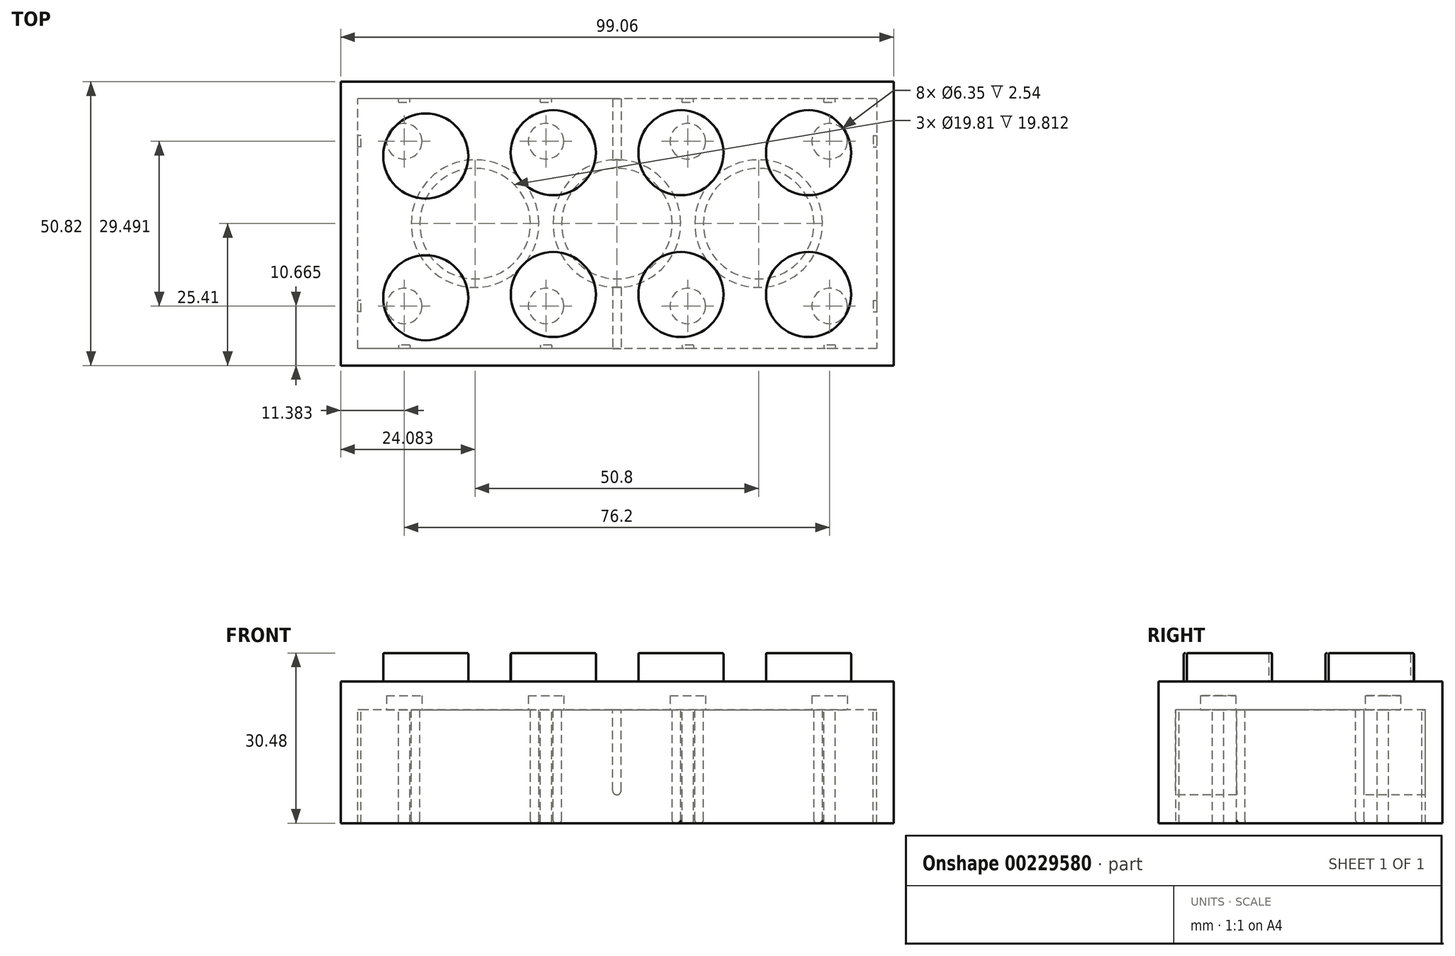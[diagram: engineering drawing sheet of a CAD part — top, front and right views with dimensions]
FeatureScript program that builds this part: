
annotation { "Feature Type Name" : "Feature", "Feature Type Description" : "" }
export const myFeature = defineFeature(function(context is Context, id is Id, definition is map)
    precondition{}
    {
        {
            var Q0;
            Q0=qCreatedBy(makeId("Top.planeOp"),FACE);
            var sketch = newSketch(context, id + "F0", { "sketchPlane" : qUnion([Q0])});
            skLineSegment(sketch, "E0.bottom", {"start": v(45.78, -25.41) * mm, "end": v(-53.28, -25.41) * mm});
            skLineSegment(sketch, "E0.top", {"start": v(45.78, 25.41) * mm, "end": v(-53.28, 25.41) * mm});
            skLineSegment(sketch, "E0.left", {"start": v(45.78, -25.41) * mm, "end": v(45.78, 25.41) * mm});
            skPoint(sketch, "E0.middle", {"position": v(0, 0) * mm});
            skLineSegment(sketch, "E1", {"start": v(-53.28, 25.41) * mm, "end": v(-53.28, -25.41) * mm});
            skSolve(sketch);
        }
        {
            var Q0;
            Q0=makeQuery(id+"F0.imprint","IMPRINT",FACE,{"disambiguationData":[TD([[makeQuery(id+"F0.imprint","IMPRINT",EDGE,{"derivedFrom":sQuery(id+"F0.wireOp",EDGE,"E0.bottom")}),-1.0]])]});
            extrude(context, id + "F1", {"entities" : qUnion([Q0]), "depth" : 25.4 * mm});
        }
        {
            var Q0;
            Q0=makeQuery(id+"F1.opExtrude","CAP_FACE",FACE,{"disambiguationData":[OSD([sQuery(id+"F0.wireOp",EDGE,"E0.bottom"),sQuery(id+"F0.wireOp",EDGE,"E0.top"),sQuery(id+"F0.wireOp",EDGE,"E0.left"),sQuery(id+"F0.wireOp",EDGE,"E0.right")])],"isStart":false});
            var sketch = newSketch(context, id + "F2", { "sketchPlane" : qUnion([Q0])});
            skCircle(sketch, "E2", {"center": v(-15.18, 12.7) * mm, "radius": 7.63 * mm});
            skCircle(sketch, "E3", {"center": v(7.68, 12.7) * mm, "radius": 7.62 * mm});
            skCircle(sketch, "E4", {"center": v(30.54, 12.7) * mm, "radius": 7.62 * mm});
            skCircle(sketch, "E5", {"center": v(30.54, -12.7) * mm, "radius": 7.62 * mm});
            skCircle(sketch, "E6", {"center": v(7.68, -12.7) * mm, "radius": 7.62 * mm});
            skCircle(sketch, "E7", {"center": v(-15.18, -12.7) * mm, "radius": 7.62 * mm});
            skCircle(sketch, "E8", {"center": v(-38.04, -13.3) * mm, "radius": 7.62 * mm});
            skCircle(sketch, "E9", {"center": v(-38.04, 12.1) * mm, "radius": 7.62 * mm});
            skLineSegment(sketch, "E10", {"start": v(-53.27, -12.48) * mm, "end": v(-53.27, -25.41) * mm});
            skLineSegment(sketch, "E11", {"start": v(-53.27, -12.48) * mm, "end": v(-53.27, 25.41) * mm});
            skSolve(sketch);
        }
        {
            var Q0;
            Q0=makeQuery(id+"F2.imprint","IMPRINT",FACE,{"disambiguationData":[TD([[makeQuery(id+"F2.imprint","IMPRINT",EDGE,{"derivedFrom":sQuery(id+"F2.wireOp",EDGE,"E2")}),1.0]])]});
            var Q1;
            Q1=makeQuery(id+"F2.imprint","IMPRINT",FACE,{"disambiguationData":[TD([[makeQuery(id+"F2.imprint","IMPRINT",EDGE,{"derivedFrom":sQuery(id+"F2.wireOp",EDGE,"E3")}),1.0]])]});
            var Q2;
            Q2=makeQuery(id+"F2.imprint","IMPRINT",FACE,{"disambiguationData":[TD([[makeQuery(id+"F2.imprint","IMPRINT",EDGE,{"derivedFrom":sQuery(id+"F2.wireOp",EDGE,"E4")}),1.0]])]});
            var Q3;
            Q3=makeQuery(id+"F2.imprint","IMPRINT",FACE,{"disambiguationData":[TD([[makeQuery(id+"F2.imprint","IMPRINT",EDGE,{"derivedFrom":sQuery(id+"F2.wireOp",EDGE,"E5")}),1.0]])]});
            var Q4;
            Q4=makeQuery(id+"F2.imprint","IMPRINT",FACE,{"disambiguationData":[TD([[makeQuery(id+"F2.imprint","IMPRINT",EDGE,{"derivedFrom":sQuery(id+"F2.wireOp",EDGE,"E6")}),1.0]])]});
            var Q5;
            Q5=makeQuery(id+"F2.imprint","IMPRINT",FACE,{"disambiguationData":[TD([[makeQuery(id+"F2.imprint","IMPRINT",EDGE,{"derivedFrom":sQuery(id+"F2.wireOp",EDGE,"E7")}),1.0]])]});
            var Q6;
            Q6=makeQuery(id+"F2.imprint","IMPRINT",FACE,{"disambiguationData":[TD([[makeQuery(id+"F2.imprint","IMPRINT",EDGE,{"derivedFrom":sQuery(id+"F2.wireOp",EDGE,"E8")}),1.0]])]});
            var Q7;
            Q7=makeQuery(id+"F2.imprint","IMPRINT",FACE,{"disambiguationData":[TD([[makeQuery(id+"F2.imprint","IMPRINT",EDGE,{"derivedFrom":sQuery(id+"F2.wireOp",EDGE,"E9")}),1.0]])]});
            extrude(context, id + "F3", {"entities" : qUnion([Q0, Q1, Q2, Q3, Q4, Q5, Q6, Q7]), "operationType" : NewBodyOperationType.ADD, "endBound" : BoundingType.SYMMETRIC, "depth" : 10.16 * mm});
        }
        {
            var Q0;
            Q0=makeQuery(id+"F1.opExtrude","CAP_FACE",FACE,{"disambiguationData":[OSD([sQuery(id+"F0.wireOp",EDGE,"E0.bottom"),sQuery(id+"F0.wireOp",EDGE,"E0.top"),sQuery(id+"F0.wireOp",EDGE,"E0.left"),sQuery(id+"F0.wireOp",EDGE,"E1")])],"isStart":true});
            var sketch = newSketch(context, id + "F4", { "sketchPlane" : qUnion([Q0])});
            skLineSegment(sketch, "E12.bottom", {"start": v(42.73, -22.37) * mm, "end": v(-50.24, -22.37) * mm});
            skLineSegment(sketch, "E13", {"start": v(42.73, -22.37) * mm, "end": v(42.73, 22.37) * mm});
            skLineSegment(sketch, "E14", {"start": v(42.73, 22.37) * mm, "end": v(-50.24, 22.37) * mm});
            skLineSegment(sketch, "E15", {"start": v(-50.24, 22.37) * mm, "end": v(-50.24, -22.37) * mm});
            skPoint(sketch, "E16.endSnap0", {"position": v(-50.24, 0) * mm});
            skSolve(sketch);
        }
        {
            var Q0;
            Q0=makeQuery(id+"F4.imprint","IMPRINT",FACE,{"disambiguationData":[TD([[makeQuery(id+"F4.imprint","IMPRINT",EDGE,{"derivedFrom":sQuery(id+"F4.wireOp",EDGE,"E12.bottom")}),-1.0]])]});
            extrude(context, id + "F5", {"entities" : qUnion([Q0]), "operationType" : NewBodyOperationType.REMOVE, "oppositeDirection" : true, "depth" : 20.32 * mm});
        }
        {
            var Q0;
            Q0=makeQuery(id+"F5.boolean.opBoolean","COPY",FACE,{"derivedFrom":makeQuery(id+"F5.opExtrude","CAP_FACE",FACE,{"disambiguationData":[OSD([sQuery(id+"F4.wireOp",EDGE,"E12.bottom"),sQuery(id+"F4.wireOp",EDGE,"E13"),sQuery(id+"F4.wireOp",EDGE,"E14"),sQuery(id+"F4.wireOp",EDGE,"E15")])],"isStart":false})});
            var sketch = newSketch(context, id + "F6", { "sketchPlane" : qUnion([Q0])});
            skPoint(sketch, "E17.endSnap0", {"position": v(-50.24, 0) * mm});
            skLineSegment(sketch, "E18.0", {"start": v(-4.56, -22.37) * mm, "end": v(-4.56, -11.4) * mm});
            skLineSegment(sketch, "E19.0", {"start": v(-3.03, -22.37) * mm, "end": v(-3.03, -11.4) * mm});
            skPoint(sketch, "E20", {"position": v(-3.8, 0) * mm});
            skCircle(sketch, "E21", {"center": v(-3.8, 0) * mm, "radius": 11.43 * mm});
            skCircle(sketch, "E22.0", {"center": v(-3.8, 0) * mm, "radius": 9.9 * mm});
            skLineSegment(sketch, "E23.trimOffspring", {"start": v(-3.03, 11.4) * mm, "end": v(-3.03, 22.37) * mm});
            skLineSegment(sketch, "E24.trimOffspring", {"start": v(-4.56, 11.4) * mm, "end": v(-4.56, 22.37) * mm});
            skPoint(sketch, "E25", {"position": v(-29.2, 0) * mm});
            skCircle(sketch, "E26", {"center": v(-29.2, 0) * mm, "radius": 9.9 * mm});
            skCircle(sketch, "E27.0", {"center": v(-29.2, 0) * mm, "radius": 11.43 * mm});
            skCircle(sketch, "E28", {"center": v(-16.5, 14.75) * mm, "radius": 3.18 * mm});
            skPoint(sketch, "E29", {"position": v(-16.5, -14.75) * mm});
            skCircle(sketch, "E30", {"center": v(-16.5, -14.75) * mm, "radius": 3.18 * mm});
            skPoint(sketch, "E31", {"position": v(-41.9, 14.75) * mm});
            skPoint(sketch, "E32", {"position": v(-41.9, -14.75) * mm});
            skCircle(sketch, "E33", {"center": v(-41.9, -14.75) * mm, "radius": 3.18 * mm});
            skCircle(sketch, "E34", {"center": v(-41.9, 14.75) * mm, "radius": 3.18 * mm});
            skCircle(sketch, "E35", {"center": v(8.9, 14.75) * mm, "radius": 3.18 * mm});
            skCircle(sketch, "E36", {"center": v(8.9, -14.75) * mm, "radius": 3.18 * mm});
            skPoint(sketch, "E37", {"position": v(21.6, 0) * mm});
            skCircle(sketch, "E38", {"center": v(21.6, 0) * mm, "radius": 9.9 * mm});
            skCircle(sketch, "E39", {"center": v(21.6, 0) * mm, "radius": 11.43 * mm});
            skCircle(sketch, "E40", {"center": v(34.3, 14.75) * mm, "radius": 3.18 * mm});
            skCircle(sketch, "E41", {"center": v(34.3, -14.75) * mm, "radius": 3.18 * mm});
            skPoint(sketch, "E42", {"position": v(-50.24, -14.75) * mm});
            skLineSegment(sketch, "E43.bottom", {"start": v(-49.63, -13.73) * mm, "end": v(-50.24, -13.73) * mm});
            skLineSegment(sketch, "E43.top", {"start": v(-49.63, -15.76) * mm, "end": v(-50.24, -15.76) * mm});
            skLineSegment(sketch, "E43.left", {"start": v(-49.63, -13.73) * mm, "end": v(-49.63, -15.76) * mm});
            skPoint(sketch, "E44", {"position": v(-50.24, -15.76) * mm});
            skPoint(sketch, "E45", {"position": v(-50.24, -13.73) * mm});
            skPoint(sketch, "E46", {"position": v(-50.24, 14.75) * mm});
            skLineSegment(sketch, "E47.bottom", {"start": v(-49.63, 15.76) * mm, "end": v(-50.24, 15.76) * mm});
            skLineSegment(sketch, "E47.top", {"start": v(-49.63, 13.73) * mm, "end": v(-50.24, 13.73) * mm});
            skLineSegment(sketch, "E47.left", {"start": v(-49.63, 15.76) * mm, "end": v(-49.63, 13.73) * mm});
            skPoint(sketch, "E48", {"position": v(-50.24, 13.73) * mm});
            skPoint(sketch, "E49", {"position": v(-50.24, 15.76) * mm});
            skPoint(sketch, "E50", {"position": v(-16.5, 22.37) * mm});
            skLineSegment(sketch, "E51.bottom", {"start": v(-15.48, 21.76) * mm, "end": v(-17.51, 21.76) * mm});
            skLineSegment(sketch, "E51.left", {"start": v(-15.48, 21.76) * mm, "end": v(-15.48, 22.37) * mm});
            skLineSegment(sketch, "E51.right", {"start": v(-17.51, 21.76) * mm, "end": v(-17.51, 22.37) * mm});
            skPoint(sketch, "E52", {"position": v(-17.51, 22.37) * mm});
            skPoint(sketch, "E53", {"position": v(-15.48, 22.37) * mm});
            skPoint(sketch, "E54", {"position": v(8.9, 22.37) * mm});
            skLineSegment(sketch, "E55.bottom", {"start": v(9.92, 21.76) * mm, "end": v(7.89, 21.76) * mm});
            skLineSegment(sketch, "E55.left", {"start": v(9.92, 21.76) * mm, "end": v(9.92, 22.37) * mm});
            skLineSegment(sketch, "E55.right", {"start": v(7.89, 21.76) * mm, "end": v(7.89, 22.37) * mm});
            skPoint(sketch, "E56", {"position": v(7.89, 22.37) * mm});
            skPoint(sketch, "E57", {"position": v(9.92, 22.37) * mm});
            skPoint(sketch, "E58", {"position": v(-41.9, 22.37) * mm});
            skLineSegment(sketch, "E59.bottom", {"start": v(-40.88, 21.76) * mm, "end": v(-42.91, 21.76) * mm});
            skLineSegment(sketch, "E59.left", {"start": v(-40.88, 21.76) * mm, "end": v(-40.88, 22.37) * mm});
            skLineSegment(sketch, "E59.right", {"start": v(-42.91, 21.76) * mm, "end": v(-42.91, 22.37) * mm});
            skPoint(sketch, "E60", {"position": v(-42.91, 22.37) * mm});
            skPoint(sketch, "E61", {"position": v(-40.88, 22.37) * mm});
            skPoint(sketch, "E62", {"position": v(34.3, 22.37) * mm});
            skLineSegment(sketch, "E63.bottom", {"start": v(35.32, 21.76) * mm, "end": v(33.29, 21.76) * mm});
            skLineSegment(sketch, "E63.left", {"start": v(35.32, 21.76) * mm, "end": v(35.32, 22.37) * mm});
            skLineSegment(sketch, "E63.right", {"start": v(33.29, 21.76) * mm, "end": v(33.29, 22.37) * mm});
            skPoint(sketch, "E64", {"position": v(33.29, 22.37) * mm});
            skPoint(sketch, "E65", {"position": v(35.32, 22.37) * mm});
            skPoint(sketch, "E66", {"position": v(42.73, 14.75) * mm});
            skLineSegment(sketch, "E67.bottom", {"start": v(42.13, 13.73) * mm, "end": v(42.73, 13.73) * mm});
            skLineSegment(sketch, "E67.top", {"start": v(42.13, 15.76) * mm, "end": v(42.73, 15.76) * mm});
            skLineSegment(sketch, "E67.left", {"start": v(42.13, 13.73) * mm, "end": v(42.13, 15.76) * mm});
            skPoint(sketch, "E68", {"position": v(42.73, 15.76) * mm});
            skPoint(sketch, "E69", {"position": v(42.73, 13.73) * mm});
            skPoint(sketch, "E70", {"position": v(42.73, -14.75) * mm});
            skLineSegment(sketch, "E71.bottom", {"start": v(42.13, -15.76) * mm, "end": v(42.73, -15.76) * mm});
            skLineSegment(sketch, "E71.top", {"start": v(42.13, -13.73) * mm, "end": v(42.73, -13.73) * mm});
            skLineSegment(sketch, "E71.left", {"start": v(42.13, -15.76) * mm, "end": v(42.13, -13.73) * mm});
            skPoint(sketch, "E72", {"position": v(42.73, -13.73) * mm});
            skPoint(sketch, "E73", {"position": v(42.73, -15.76) * mm});
            skPoint(sketch, "E74", {"position": v(34.3, -22.37) * mm});
            skLineSegment(sketch, "E75.bottom", {"start": v(33.29, -21.76) * mm, "end": v(35.32, -21.76) * mm});
            skLineSegment(sketch, "E75.left", {"start": v(33.29, -21.76) * mm, "end": v(33.29, -22.37) * mm});
            skLineSegment(sketch, "E75.right", {"start": v(35.32, -21.76) * mm, "end": v(35.32, -22.37) * mm});
            skPoint(sketch, "E76", {"position": v(35.32, -22.37) * mm});
            skPoint(sketch, "E77", {"position": v(33.29, -22.37) * mm});
            skPoint(sketch, "E78", {"position": v(8.9, -22.37) * mm});
            skLineSegment(sketch, "E79.bottom", {"start": v(7.89, -21.76) * mm, "end": v(9.92, -21.76) * mm});
            skLineSegment(sketch, "E79.left", {"start": v(7.89, -21.76) * mm, "end": v(7.89, -22.37) * mm});
            skLineSegment(sketch, "E79.right", {"start": v(9.92, -21.76) * mm, "end": v(9.92, -22.37) * mm});
            skPoint(sketch, "E80", {"position": v(9.92, -22.37) * mm});
            skPoint(sketch, "E81", {"position": v(7.89, -22.37) * mm});
            skPoint(sketch, "E82", {"position": v(-16.5, -22.37) * mm});
            skLineSegment(sketch, "E83.bottom", {"start": v(-17.51, -21.76) * mm, "end": v(-15.48, -21.76) * mm});
            skLineSegment(sketch, "E83.left", {"start": v(-17.51, -21.76) * mm, "end": v(-17.51, -22.37) * mm});
            skLineSegment(sketch, "E83.right", {"start": v(-15.48, -21.76) * mm, "end": v(-15.48, -22.37) * mm});
            skPoint(sketch, "E84", {"position": v(-15.48, -22.37) * mm});
            skPoint(sketch, "E85", {"position": v(-17.51, -22.37) * mm});
            skPoint(sketch, "E86", {"position": v(-41.9, -22.37) * mm});
            skLineSegment(sketch, "E87.bottom", {"start": v(-42.91, -21.76) * mm, "end": v(-40.88, -21.76) * mm});
            skLineSegment(sketch, "E87.left", {"start": v(-42.91, -21.76) * mm, "end": v(-42.91, -22.37) * mm});
            skLineSegment(sketch, "E87.right", {"start": v(-40.88, -21.76) * mm, "end": v(-40.88, -22.37) * mm});
            skPoint(sketch, "E88", {"position": v(-40.88, -22.37) * mm});
            skPoint(sketch, "E89", {"position": v(-42.91, -22.37) * mm});
            skSolve(sketch);
        }
        {
            var Q0;
            {var subQ0=sQuery(id+"F6.wireOp",EDGE,"E18.0");Q0=makeQuery(id+"F6.imprint","IMPRINT",FACE,{"disambiguationData":[TD([[makeQuery(id+"F6.imprint","IMPRINT",EDGE,{"derivedFrom":subQ0}),-1.0]])]});}
            extrude(context, id + "F7", {"entities" : qUnion([Q0]), "operationType" : NewBodyOperationType.ADD, "depth" : 15.24 * mm});
        }
        {
            var Q0;
            Q0=makeQuery(id+"F7.opExtrude","CAP_EDGE",EDGE,{"disambiguationData":[OSD([sQuery(id+"F6.wireOp",EDGE,"E19.0")])],"isStart":false});
            var Q1;
            Q1=makeQuery(id+"F7.opExtrude","CAP_EDGE",EDGE,{"disambiguationData":[OSD([sQuery(id+"F6.wireOp",EDGE,"E18.0")])],"isStart":false});
            fillet(context, id + "F8", {"entities" : qUnion([Q0, Q1]), "radius" : 0.76 * mm, "tangentPropagation" : true, "allowEdgeOverflow" : false});
        }
        {
            var Q0;
            {var subQ0=sQuery(id+"F6.wireOp",EDGE,"E23.trimOffspring");Q0=makeQuery(id+"F6.imprint","IMPRINT",FACE,{"disambiguationData":[TD([[makeQuery(id+"F6.imprint","IMPRINT",EDGE,{"derivedFrom":subQ0}),1.0]])]});}
            extrude(context, id + "F9", {"entities" : qUnion([Q0]), "operationType" : NewBodyOperationType.ADD, "depth" : 15.24 * mm});
        }
        {
            var Q0;
            Q0=makeQuery(id+"F9.opExtrude","CAP_EDGE",EDGE,{"disambiguationData":[OSD([sQuery(id+"F6.wireOp",EDGE,"E23.trimOffspring")])],"isStart":false});
            var Q1;
            Q1=makeQuery(id+"F9.opExtrude","CAP_EDGE",EDGE,{"disambiguationData":[OSD([sQuery(id+"F6.wireOp",EDGE,"E24.trimOffspring")])],"isStart":false});
            fillet(context, id + "F10", {"entities" : qUnion([Q0, Q1]), "radius" : 0.76 * mm, "tangentPropagation" : true, "allowEdgeOverflow" : false});
        }
        {
            var Q0;
            Q0=makeQuery(id+"F6.imprint","IMPRINT",FACE,{"disambiguationData":[TD([[makeQuery(id+"F6.imprint","IMPRINT",EDGE,{"derivedFrom":sQuery(id+"F6.wireOp",EDGE,"E22.0")}),-1.0]])]});
            var Q1;
            Q1=makeQuery(id+"F6.imprint","IMPRINT",FACE,{"disambiguationData":[TD([[makeQuery(id+"F6.imprint","IMPRINT",EDGE,{"derivedFrom":sQuery(id+"F6.wireOp",EDGE,"Xv8gO2pj-0vQc-Pp1w-HGMN-q8keW2Wz2Wm3")}),-1.0]])]});
            var Q2;
            Q2=makeQuery(id+"F6.imprint","IMPRINT",FACE,{"disambiguationData":[TD([[makeQuery(id+"F6.imprint","IMPRINT",EDGE,{"derivedFrom":sQuery(id+"F6.wireOp",EDGE,"E26")}),-1.0]])]});
            var Q3;
            Q3=makeQuery(id+"F6.imprint","IMPRINT",FACE,{"disambiguationData":[TD([[makeQuery(id+"F6.imprint","IMPRINT",EDGE,{"derivedFrom":sQuery(id+"F6.wireOp",EDGE,"E38")}),-1.0]])]});
            var Q4;
            Q4=makeQuery(id+"F6.imprint","IMPRINT",FACE,{"disambiguationData":[TD([[makeQuery(id+"F6.imprint","IMPRINT",EDGE,{"derivedFrom":sQuery(id+"F6.wireOp",EDGE,"E63.bottom")}),-1.0]])]});
            var Q5;
            {var subQ0=sQuery(id+"F6.wireOp",EDGE,"E67.bottom");Q5=makeQuery(id+"F6.imprint","IMPRINT",FACE,{"disambiguationData":[TD([[makeQuery(id+"F6.imprint","IMPRINT",EDGE,{"derivedFrom":subQ0}),1.0]])]});}
            var Q6;
            {var subQ0=sQuery(id+"F6.wireOp",EDGE,"E71.bottom");Q6=makeQuery(id+"F6.imprint","IMPRINT",FACE,{"disambiguationData":[TD([[makeQuery(id+"F6.imprint","IMPRINT",EDGE,{"derivedFrom":subQ0}),1.0]])]});}
            var Q7;
            Q7=makeQuery(id+"F6.imprint","IMPRINT",FACE,{"disambiguationData":[TD([[makeQuery(id+"F6.imprint","IMPRINT",EDGE,{"derivedFrom":sQuery(id+"F6.wireOp",EDGE,"E75.bottom")}),-1.0]])]});
            var Q8;
            Q8=makeQuery(id+"F6.imprint","IMPRINT",FACE,{"disambiguationData":[TD([[makeQuery(id+"F6.imprint","IMPRINT",EDGE,{"derivedFrom":sQuery(id+"F6.wireOp",EDGE,"E79.bottom")}),-1.0]])]});
            var Q9;
            Q9=makeQuery(id+"F6.imprint","IMPRINT",FACE,{"disambiguationData":[TD([[makeQuery(id+"F6.imprint","IMPRINT",EDGE,{"derivedFrom":sQuery(id+"F6.wireOp",EDGE,"E83.bottom")}),-1.0]])]});
            var Q10;
            Q10=makeQuery(id+"F6.imprint","IMPRINT",FACE,{"disambiguationData":[TD([[makeQuery(id+"F6.imprint","IMPRINT",EDGE,{"derivedFrom":sQuery(id+"F6.wireOp",EDGE,"E87.bottom")}),-1.0]])]});
            var Q11;
            {var subQ0=sQuery(id+"F6.wireOp",EDGE,"E43.bottom");Q11=makeQuery(id+"F6.imprint","IMPRINT",FACE,{"disambiguationData":[TD([[makeQuery(id+"F6.imprint","IMPRINT",EDGE,{"derivedFrom":subQ0}),1.0]])]});}
            var Q12;
            {var subQ0=sQuery(id+"F6.wireOp",EDGE,"E47.bottom");Q12=makeQuery(id+"F6.imprint","IMPRINT",FACE,{"disambiguationData":[TD([[makeQuery(id+"F6.imprint","IMPRINT",EDGE,{"derivedFrom":subQ0}),1.0]])]});}
            var Q13;
            Q13=makeQuery(id+"F6.imprint","IMPRINT",FACE,{"disambiguationData":[TD([[makeQuery(id+"F6.imprint","IMPRINT",EDGE,{"derivedFrom":sQuery(id+"F6.wireOp",EDGE,"E59.bottom")}),-1.0]])]});
            var Q14;
            Q14=makeQuery(id+"F6.imprint","IMPRINT",FACE,{"disambiguationData":[TD([[makeQuery(id+"F6.imprint","IMPRINT",EDGE,{"derivedFrom":sQuery(id+"F6.wireOp",EDGE,"E51.bottom")}),-1.0]])]});
            var Q15;
            Q15=makeQuery(id+"F6.imprint","IMPRINT",FACE,{"disambiguationData":[TD([[makeQuery(id+"F6.imprint","IMPRINT",EDGE,{"derivedFrom":sQuery(id+"F6.wireOp",EDGE,"E55.bottom")}),-1.0]])]});
            var Q16;
            Q16=sQuery(id+"F6.wireOp",EDGE,"E21");
            var Q17;
            Q17=makeQuery(id+"F5.boolean.opBoolean","COPY",FACE,{"derivedFrom":makeQuery(id+"F5.opExtrude","CAP_FACE",FACE,{"disambiguationData":[OSD([sQuery(id+"F4.wireOp",EDGE,"E12.bottom"),sQuery(id+"F4.wireOp",EDGE,"E13"),sQuery(id+"F4.wireOp",EDGE,"E14"),sQuery(id+"F4.wireOp",EDGE,"E15")])],"isStart":false})});
            var Q18;
            Q18=makeQuery(id+"F1.opExtrude","SWEPT_BODY",BODY,{"disambiguationData":[OSD([sQuery(id+"F0.wireOp",EDGE,"E0.bottom"),sQuery(id+"F0.wireOp",EDGE,"E0.top"),sQuery(id+"F0.wireOp",EDGE,"E0.left"),sQuery(id+"F0.wireOp",EDGE,"E1")])]});
            extrude(context, id + "F11", {"entities" : qUnion([Q0, Q1, Q2, Q3, Q4, Q5, Q6, Q7, Q8, Q9, Q10, Q11, Q12, Q13, Q14, Q15]), "surfaceEntities" : qUnion([Q16]), "endBoundEntityFace" : qUnion([Q17]), "endBoundEntityBody" : qUnion([Q18]), "depth" : 20.32 * mm});
        }
        {
            var Q0;
            Q0=makeQuery(id+"F11.opExtrude","CAP_EDGE",EDGE,{"disambiguationData":[OSD([sQuery(id+"F6.wireOp",EDGE,"E21")])],"isStart":false});
            var Q1;
            Q1=makeQuery(id+"F11.opExtrude","CAP_EDGE",EDGE,{"disambiguationData":[OSD([sQuery(id+"F6.wireOp",EDGE,"E27.0")])],"isStart":false});
            var Q2;
            Q2=makeQuery(id+"F11.opExtrude","CAP_EDGE",EDGE,{"disambiguationData":[OSD([sQuery(id+"F6.wireOp",EDGE,"f30a9259-305a-4341-86ed-62d9fef0a3dd.0")])],"isStart":false});
            var Q3;
            Q3=makeQuery(id+"F11.opExtrude","CAP_EDGE",EDGE,{"disambiguationData":[OSD([sQuery(id+"F6.wireOp",EDGE,"Xv8gO2pj-0vQc-Pp1w-HGMN-q8keW2Wz2Wm3")])],"isStart":false});
            var Q4;
            Q4=makeQuery(id+"F11.opExtrude","CAP_EDGE",EDGE,{"disambiguationData":[OSD([sQuery(id+"F6.wireOp",EDGE,"E26")])],"isStart":false});
            var Q5;
            Q5=makeQuery(id+"F11.opExtrude","CAP_EDGE",EDGE,{"disambiguationData":[OSD([sQuery(id+"F6.wireOp",EDGE,"E22.0")])],"isStart":false});
            var Q6;
            Q6=makeQuery(id+"F11.opExtrude","CAP_EDGE",EDGE,{"disambiguationData":[OSD([sQuery(id+"F6.wireOp",EDGE,"E39")])],"isStart":false});
            var Q7;
            Q7=makeQuery(id+"F11.opExtrude","CAP_EDGE",EDGE,{"disambiguationData":[OSD([sQuery(id+"F6.wireOp",EDGE,"E38")])],"isStart":false});
            fillet(context, id + "F12", {"entities" : qUnion([Q0, Q1, Q2, Q3, Q4, Q5, Q6, Q7]), "radius" : 0.5 * mm, "tangentPropagation" : true, "allowEdgeOverflow" : false});
        }
        {
            var Q0;
            Q0=makeQuery(id+"F6.imprint","IMPRINT",FACE,{"disambiguationData":[TD([[makeQuery(id+"F6.imprint","IMPRINT",EDGE,{"derivedFrom":sQuery(id+"F6.wireOp",EDGE,"E41")}),1.0]])]});
            var Q1;
            Q1=makeQuery(id+"F6.imprint","IMPRINT",FACE,{"disambiguationData":[TD([[makeQuery(id+"F6.imprint","IMPRINT",EDGE,{"derivedFrom":sQuery(id+"F6.wireOp",EDGE,"E36")}),1.0]])]});
            var Q2;
            Q2=makeQuery(id+"F6.imprint","IMPRINT",FACE,{"disambiguationData":[TD([[makeQuery(id+"F6.imprint","IMPRINT",EDGE,{"derivedFrom":sQuery(id+"F6.wireOp",EDGE,"E35")}),1.0]])]});
            var Q3;
            Q3=makeQuery(id+"F6.imprint","IMPRINT",FACE,{"disambiguationData":[TD([[makeQuery(id+"F6.imprint","IMPRINT",EDGE,{"derivedFrom":sQuery(id+"F6.wireOp",EDGE,"E40")}),1.0]])]});
            var Q4;
            Q4=makeQuery(id+"F6.imprint","IMPRINT",FACE,{"disambiguationData":[TD([[makeQuery(id+"F6.imprint","IMPRINT",EDGE,{"derivedFrom":sQuery(id+"F6.wireOp",EDGE,"E28")}),1.0]])]});
            var Q5;
            Q5=makeQuery(id+"F6.imprint","IMPRINT",FACE,{"disambiguationData":[TD([[makeQuery(id+"F6.imprint","IMPRINT",EDGE,{"derivedFrom":sQuery(id+"F6.wireOp",EDGE,"E30")}),1.0]])]});
            var Q6;
            Q6=makeQuery(id+"F6.imprint","IMPRINT",FACE,{"disambiguationData":[TD([[makeQuery(id+"F6.imprint","IMPRINT",EDGE,{"derivedFrom":sQuery(id+"F6.wireOp",EDGE,"E34")}),1.0]])]});
            var Q7;
            Q7=makeQuery(id+"F6.imprint","IMPRINT",FACE,{"disambiguationData":[TD([[makeQuery(id+"F6.imprint","IMPRINT",EDGE,{"derivedFrom":sQuery(id+"F6.wireOp",EDGE,"E33")}),1.0]])]});
            extrude(context, id + "F13", {"entities" : qUnion([Q0, Q1, Q2, Q3, Q4, Q5, Q6, Q7]), "operationType" : NewBodyOperationType.REMOVE, "oppositeDirection" : true, "depth" : 2.54 * mm});
        }
        {
            var Q0;
            Q0=makeQuery(id+"F3.opExtrude","CAP_EDGE",EDGE,{"disambiguationData":[OSD([sQuery(id+"F2.wireOp",EDGE,"E7")])],"isStart":false});
            var Q1;
            Q1=makeQuery(id+"F3.opExtrude","CAP_EDGE",EDGE,{"disambiguationData":[OSD([sQuery(id+"F2.wireOp",EDGE,"E6")])],"isStart":false});
            var Q2;
            Q2=makeQuery(id+"F3.opExtrude","CAP_EDGE",EDGE,{"disambiguationData":[OSD([sQuery(id+"F2.wireOp",EDGE,"E5")])],"isStart":false});
            var Q3;
            Q3=makeQuery(id+"F3.opExtrude","CAP_EDGE",EDGE,{"disambiguationData":[OSD([sQuery(id+"F2.wireOp",EDGE,"E4")])],"isStart":false});
            var Q4;
            Q4=makeQuery(id+"F3.opExtrude","CAP_EDGE",EDGE,{"disambiguationData":[OSD([sQuery(id+"F2.wireOp",EDGE,"E3")])],"isStart":false});
            var Q5;
            Q5=makeQuery(id+"F3.opExtrude","CAP_EDGE",EDGE,{"disambiguationData":[OSD([sQuery(id+"F2.wireOp",EDGE,"E2")])],"isStart":false});
            var Q6;
            Q6=makeQuery(id+"F3.opExtrude","CAP_EDGE",EDGE,{"disambiguationData":[OSD([sQuery(id+"F2.wireOp",EDGE,"E9")])],"isStart":false});
            var Q7;
            Q7=makeQuery(id+"F3.opExtrude","CAP_EDGE",EDGE,{"disambiguationData":[OSD([sQuery(id+"F2.wireOp",EDGE,"E8")])],"isStart":false});
            fillet(context, id + "F14", {"entities" : qUnion([Q0, Q1, Q2, Q3, Q4, Q5, Q6, Q7]), "radius" : 0.25 * mm, "tangentPropagation" : true, "allowEdgeOverflow" : false});
        }
    });
